FCSTD DOCUMENT  (FreeCAD 0.20R29177 +426 (Git))
Label: layout
License: All rights reserved
LicenseURL: http://en.wikipedia.org/wiki/All_rights_reserved
objects: Sketcher::SketchObject×3
note: 3 computed .brp shape members not serialized (recipe doc carries the construction recipe); baked Part::Feature solids carry a one-line shape summary decoded from their .brp

FEATURE [Sketcher::SketchObject] Sketch
  FullyConstrained = true
  sketch-geometry (256):
    g0: Circle CenterX=165.971 CenterY=76.4159 CenterZ=0 NormalX=0 NormalY=0 NormalZ=1 AngleXU=0 Radius=12
    g1: Circle CenterX=195.971 CenterY=76.4159 CenterZ=0 NormalX=0 NormalY=0 NormalZ=1 AngleXU=0 Radius=12
    g2: Circle CenterX=165.971 CenterY=106.416 CenterZ=0 NormalX=0 NormalY=0 NormalZ=1 AngleXU=0 Radius=12
    g3: Circle CenterX=195.971 CenterY=106.416 CenterZ=0 NormalX=0 NormalY=0 NormalZ=1 AngleXU=0 Radius=12
    g4: Circle CenterX=225.019 CenterY=98.9159 CenterZ=0 NormalX=0 NormalY=0 NormalZ=1 AngleXU=0 Radius=12
    g5: Circle CenterX=225.019 CenterY=68.9159 CenterZ=0 NormalX=0 NormalY=0 NormalZ=1 AngleXU=0 Radius=12
    g6: Circle CenterX=139.99 CenterY=91.4159 CenterZ=0 NormalX=0 NormalY=0 NormalZ=1 AngleXU=0 Radius=12
    g7: Circle CenterX=139.99 CenterY=61.4159 CenterZ=0 NormalX=0 NormalY=0 NormalZ=1 AngleXU=0 Radius=12
    g8: Circle CenterX=114.01 CenterY=76.4159 CenterZ=0 NormalX=0 NormalY=0 NormalZ=1 AngleXU=0 Radius=12
    g9: Circle CenterX=88.0289 CenterY=91.4159 CenterZ=0 NormalX=0 NormalY=0 NormalZ=1 AngleXU=0 Radius=12
    g10: Circle CenterX=58.0289 CenterY=91.4159 CenterZ=0 NormalX=0 NormalY=0 NormalZ=1 AngleXU=0 Radius=12
    g11: Circle CenterX=127 CenterY=23.5841 CenterZ=0 NormalX=0 NormalY=0 NormalZ=1 AngleXU=0 Radius=15
    g12: LineSegment StartX=139.99 StartY=61.4159 StartZ=0 EndX=88.0289 EndY=91.4159 EndZ=0
    g13: LineSegment StartX=139.99 StartY=61.4159 StartZ=0 EndX=127 EndY=61.4159 EndZ=0
    g14: LineSegment StartX=127 StartY=61.4159 StartZ=0 EndX=114.01 EndY=61.4159 EndZ=0
    g15: LineSegment StartX=10 StartY=127 StartZ=0 EndX=244 EndY=127 EndZ=0
    g16: LineSegment StartX=254 StartY=117 StartZ=0 EndX=254 EndY=10 EndZ=0
    g17: LineSegment StartX=244 StartY=0 StartZ=0 EndX=10 EndY=0 EndZ=0
    g18: LineSegment StartX=0 StartY=10 StartZ=0 EndX=0 EndY=117 EndZ=0
    g19: LineSegment StartX=127 StartY=23.5841 StartZ=0 EndX=0 EndY=23.5841 EndZ=0
    g20: LineSegment StartX=127 StartY=23.5841 StartZ=0 EndX=254 EndY=23.5841 EndZ=0
    g21: LineSegment StartX=58.0289 StartY=91.4159 StartZ=0 EndX=88.0289 EndY=91.4159 EndZ=0
    g22: LineSegment StartX=114.01 StartY=76.4159 StartZ=0 EndX=139.99 EndY=91.4159 EndZ=0
    g23: LineSegment StartX=139.99 StartY=91.4159 StartZ=0 EndX=165.971 EndY=106.416 EndZ=0
    g24: LineSegment StartX=165.971 StartY=106.416 StartZ=0 EndX=195.971 EndY=106.416 EndZ=0
    g25: LineSegment StartX=195.971 StartY=106.416 StartZ=0 EndX=225.019 EndY=98.9159 EndZ=0
    g26: LineSegment StartX=225.019 StartY=98.9159 StartZ=0 EndX=225.019 EndY=68.9159 EndZ=0
    g27: LineSegment StartX=165.971 StartY=106.416 StartZ=0 EndX=165.971 EndY=76.4159 EndZ=0
    g28: LineSegment StartX=139.99 StartY=91.4159 StartZ=0 EndX=139.99 EndY=61.4159 EndZ=0
    g29: LineSegment StartX=139.99 StartY=61.4159 StartZ=0 EndX=127 EndY=23.5841 EndZ=0
    g30: Circle CenterX=28.9815 CenterY=83.9159 CenterZ=0 NormalX=0 NormalY=0 NormalZ=1 AngleXU=0 Radius=12
    g31: Circle CenterX=28.9815 CenterY=53.9159 CenterZ=0 NormalX=0 NormalY=0 NormalZ=1 AngleXU=0 Radius=12
    g32: Circle CenterX=58.0289 CenterY=61.4159 CenterZ=0 NormalX=0 NormalY=0 NormalZ=1 AngleXU=0 Radius=12
    g33: Circle CenterX=88.0289 CenterY=61.4159 CenterZ=0 NormalX=0 NormalY=0 NormalZ=1 AngleXU=0 Radius=12
    g34: LineSegment StartX=58.0289 StartY=91.4159 StartZ=0 EndX=28.9815 EndY=83.9159 EndZ=0
    g35: LineSegment StartX=28.9815 StartY=83.9159 StartZ=0 EndX=28.9815 EndY=53.9159 EndZ=0
    g36: LineSegment StartX=58.0289 StartY=91.4159 StartZ=0 EndX=58.0289 EndY=61.4159 EndZ=0
    g37: LineSegment StartX=88.0289 StartY=91.4159 StartZ=0 EndX=88.0289 EndY=61.4159 EndZ=0
    g38: ArcOfCircle CenterX=10 CenterY=117 CenterZ=0 NormalX=0 NormalY=0 NormalZ=1 AngleXU=0 Radius=10 StartAngle=1.5708 EndAngle=3.14159
    g39: ArcOfCircle CenterX=10 CenterY=10 CenterZ=0 NormalX=0 NormalY=0 NormalZ=1 AngleXU=0 Radius=10 StartAngle=3.14159 EndAngle=4.71239
    g40: ArcOfCircle CenterX=244 CenterY=10 CenterZ=0 NormalX=0 NormalY=0 NormalZ=1 AngleXU=0 Radius=10 StartAngle=4.71239 EndAngle=6.28319
    g41: ArcOfCircle CenterX=244 CenterY=117 CenterZ=0 NormalX=0 NormalY=0 NormalZ=1 AngleXU=0 Radius=10 StartAngle=0 EndAngle=1.5708
    g42: LineSegment StartX=127 StartY=8.58407 StartZ=0 EndX=127 EndY=0 EndZ=0
    g43: LineSegment StartX=165.971 StartY=118.416 StartZ=0 EndX=165.971 EndY=127 EndZ=0
    g44: LineSegment StartX=17.522 StartY=119.1 StartZ=0 EndX=44.422 EndY=119.1 EndZ=0
    g45: LineSegment StartX=44.422 StartY=119.1 StartZ=0 EndX=44.422 EndY=99.64 EndZ=0
    g46: LineSegment StartX=44.422 StartY=99.64 StartZ=0 EndX=17.522 EndY=99.64 EndZ=0
    g47: LineSegment StartX=17.522 StartY=99.64 StartZ=0 EndX=17.522 EndY=119.1 EndZ=0
    g48: Circle CenterX=157.215 CenterY=36.8533 CenterZ=0 NormalX=0 NormalY=0 NormalZ=1 AngleXU=0 Radius=12
    g49: Circle CenterX=94.1366 CenterY=26.5841 CenterZ=0 NormalX=0 NormalY=0 NormalZ=1 AngleXU=0 Radius=12
    g50: LineSegment StartX=94.1366 StartY=26.5841 StartZ=0 EndX=127 EndY=23.5841 EndZ=0
    g51: LineSegment StartX=109.54 StartY=127 StartZ=0 EndX=118.48 EndY=127 EndZ=0
    g52: LineSegment StartX=118.48 StartY=127 StartZ=0 EndX=118.48 EndY=119.41 EndZ=0
    g53: LineSegment StartX=118.48 StartY=119.41 StartZ=0 EndX=109.54 EndY=119.41 EndZ=0
    g54: LineSegment StartX=109.54 StartY=119.41 StartZ=0 EndX=109.54 EndY=127 EndZ=0
    g55: LineSegment StartX=81.9846 StartY=127 StartZ=0 EndX=95.2346 EndY=127 EndZ=0
    g56: LineSegment StartX=95.2346 StartY=127 StartZ=0 EndX=95.2346 EndY=118.4 EndZ=0
    g57: LineSegment StartX=95.2346 StartY=118.4 StartZ=0 EndX=81.9846 EndY=118.4 EndZ=0
    g58: LineSegment StartX=81.9846 StartY=118.4 StartZ=0 EndX=81.9846 EndY=127 EndZ=0
    g59: LineSegment StartX=17.522 StartY=127 StartZ=0 EndX=25.372 EndY=127 EndZ=0
    g60: LineSegment StartX=25.372 StartY=127 StartZ=0 EndX=25.372 EndY=123.25 EndZ=0
    g61: LineSegment StartX=25.372 StartY=123.25 StartZ=0 EndX=17.522 EndY=123.25 EndZ=0
    g62: LineSegment StartX=17.522 StartY=123.25 StartZ=0 EndX=17.522 EndY=127 EndZ=0
    g63: LineSegment StartX=20 StartY=117 StartZ=0 EndX=41.744 EndY=117 EndZ=0
    g64: LineSegment StartX=41.744 StartY=117 StartZ=0 EndX=41.744 EndY=106.136 EndZ=0
    g65: LineSegment StartX=41.744 StartY=106.136 StartZ=0 EndX=20 EndY=106.136 EndZ=0
    g66: LineSegment StartX=20 StartY=106.136 StartZ=0 EndX=20 EndY=117 EndZ=0
    g67: LineSegment StartX=109.54 StartY=124.41 StartZ=0 EndX=114.01 EndY=124.41 EndZ=0
    g68: LineSegment StartX=114.01 StartY=124.41 StartZ=0 EndX=118.48 EndY=124.41 EndZ=0
    g69: LineSegment StartX=95.2346 StartY=123.4 StartZ=0 EndX=88.6096 EndY=123.4 EndZ=0
    g70: LineSegment StartX=88.6096 StartY=123.4 StartZ=0 EndX=81.9846 EndY=123.4 EndZ=0
    g71: LineSegment StartX=88.0289 StartY=61.4159 StartZ=0 EndX=94.1366 EndY=26.5841 EndZ=0
    g72: LineSegment StartX=157.215 StartY=36.8533 StartZ=0 EndX=127 EndY=23.5841 EndZ=0
    g73: LineSegment StartX=139.99 StartY=61.4159 StartZ=0 EndX=157.215 EndY=36.8533 EndZ=0
    g74: LineSegment StartX=36.572 StartY=127 StartZ=0 EndX=44.422 EndY=127 EndZ=0
    g75: LineSegment StartX=44.422 StartY=127 StartZ=0 EndX=44.422 EndY=123.25 EndZ=0
    g76: LineSegment StartX=44.422 StartY=123.25 StartZ=0 EndX=36.572 EndY=123.25 EndZ=0
    g77: LineSegment StartX=36.572 StartY=123.25 StartZ=0 EndX=36.572 EndY=127 EndZ=0
    g78: Circle CenterX=10 CenterY=117 CenterZ=0 NormalX=0 NormalY=0 NormalZ=1 AngleXU=0 Radius=2
    g79: Circle CenterX=244 CenterY=117 CenterZ=0 NormalX=0 NormalY=0 NormalZ=1 AngleXU=0 Radius=2
    g80: Circle CenterX=244 CenterY=10 CenterZ=0 NormalX=0 NormalY=0 NormalZ=1 AngleXU=0 Radius=2
    g81: Circle CenterX=10 CenterY=10 CenterZ=0 NormalX=0 NormalY=0 NormalZ=1 AngleXU=0 Radius=2
    g82: Circle CenterX=109.191 CenterY=10 CenterZ=0 NormalX=0 NormalY=0 NormalZ=1 AngleXU=0 Radius=2
    g83: Circle CenterX=144.809 CenterY=117 CenterZ=0 NormalX=0 NormalY=0 NormalZ=1 AngleXU=0 Radius=2
    g84: LineSegment StartX=127 StartY=23.5841 StartZ=0 EndX=109.191 EndY=10 EndZ=0
    g85: LineSegment StartX=109.191 StartY=10 StartZ=0 EndX=94.1366 EndY=26.5841 EndZ=0
    g86: LineSegment StartX=144.809 StartY=117 StartZ=0 EndX=127 EndY=117 EndZ=0
    g87: LineSegment StartX=109.191 StartY=10 StartZ=0 EndX=127 EndY=10 EndZ=0
    g88: LineSegment StartX=23.172 StartY=98.48 StartZ=0 EndX=38.772 EndY=98.48 EndZ=0
    g89: LineSegment StartX=38.772 StartY=98.48 StartZ=0 EndX=44.422 EndY=98.48 EndZ=0
    g90: LineSegment StartX=23.172 StartY=98.48 StartZ=0 EndX=17.522 EndY=98.48 EndZ=0
    g91: LineSegment StartX=23.172 StartY=98.48 StartZ=0 EndX=23.172 EndY=108.71 EndZ=0
    g92: LineSegment StartX=23.172 StartY=108.71 StartZ=0 EndX=38.772 EndY=108.71 EndZ=0
    g93: LineSegment StartX=38.772 StartY=108.71 StartZ=0 EndX=38.772 EndY=98.48 EndZ=0
    g94: ArcOfCircle CenterX=23.172 CenterY=98.48 CenterZ=0 NormalX=0 NormalY=0 NormalZ=1 AngleXU=0 Radius=0.5 StartAngle=1.5708 EndAngle=4.71239
    g95: ArcOfCircle CenterX=38.772 CenterY=98.48 CenterZ=0 NormalX=0 NormalY=0 NormalZ=1 AngleXU=0 Radius=0.5 StartAngle=4.71239 EndAngle=7.85398
    g96: LineSegment StartX=23.172 StartY=97.98 StartZ=0 EndX=38.772 EndY=97.98 EndZ=0
    g97: LineSegment StartX=23.172 StartY=98.98 StartZ=0 EndX=38.772 EndY=98.98 EndZ=0
    g98: Circle CenterX=10 CenterY=117 CenterZ=0 NormalX=0 NormalY=0 NormalZ=1 AngleXU=0 Radius=1.3
    g99: Circle CenterX=144.809 CenterY=117 CenterZ=0 NormalX=0 NormalY=0 NormalZ=1 AngleXU=0 Radius=1.3
    g100: Circle CenterX=244 CenterY=117 CenterZ=0 NormalX=0 NormalY=0 NormalZ=1 AngleXU=0 Radius=1.3
    g101: Circle CenterX=244 CenterY=10 CenterZ=0 NormalX=0 NormalY=0 NormalZ=1 AngleXU=0 Radius=1.3
    g102: Circle CenterX=109.191 CenterY=10 CenterZ=0 NormalX=0 NormalY=0 NormalZ=1 AngleXU=0 Radius=1.3
    g103: Circle CenterX=10 CenterY=10 CenterZ=0 NormalX=0 NormalY=0 NormalZ=1 AngleXU=0 Radius=1.3
    g104: LineSegment StartX=17.522 StartY=119.6 StartZ=0 EndX=44.422 EndY=119.6 EndZ=0
    g105: LineSegment StartX=44.922 StartY=119.1 StartZ=0 EndX=44.922 EndY=98.48 EndZ=0
    g106: LineSegment StartX=44.422 StartY=97.98 StartZ=0 EndX=17.522 EndY=97.98 EndZ=0
    g107: LineSegment StartX=17.022 StartY=98.48 StartZ=0 EndX=17.022 EndY=119.1 EndZ=0
    g108: ArcOfCircle CenterX=44.422 CenterY=119.1 CenterZ=0 NormalX=0 NormalY=0 NormalZ=1 AngleXU=0 Radius=0.5 StartAngle=7.2e-15 EndAngle=1.5708
    g109: ArcOfCircle CenterX=44.422 CenterY=98.48 CenterZ=0 NormalX=0 NormalY=0 NormalZ=1 AngleXU=0 Radius=0.5 StartAngle=4.71239 EndAngle=6.28319
    g110: ArcOfCircle CenterX=17.522 CenterY=98.48 CenterZ=0 NormalX=0 NormalY=0 NormalZ=1 AngleXU=0 Radius=0.5 StartAngle=3.14159 EndAngle=4.71239
    g111: ArcOfCircle CenterX=17.522 CenterY=119.1 CenterZ=0 NormalX=0 NormalY=0 NormalZ=1 AngleXU=0 Radius=0.5 StartAngle=1.5708 EndAngle=3.14159
    g112: Circle CenterX=28.9815 CenterY=83.9159 CenterZ=0 NormalX=0 NormalY=0 NormalZ=1 AngleXU=0 Radius=11
    g113: Circle CenterX=58.0289 CenterY=91.4159 CenterZ=0 NormalX=0 NormalY=0 NormalZ=1 AngleXU=0 Radius=11
    g114: Circle CenterX=28.9815 CenterY=53.9159 CenterZ=0 NormalX=0 NormalY=0 NormalZ=1 AngleXU=0 Radius=11
    g115: Circle CenterX=58.0289 CenterY=61.4159 CenterZ=0 NormalX=0 NormalY=0 NormalZ=1 AngleXU=0 Radius=11
    g116: Circle CenterX=88.0289 CenterY=61.4159 CenterZ=0 NormalX=0 NormalY=0 NormalZ=1 AngleXU=0 Radius=11
    g117: Circle CenterX=88.0289 CenterY=91.4159 CenterZ=0 NormalX=0 NormalY=0 NormalZ=1 AngleXU=0 Radius=11
    g118: Circle CenterX=114.01 CenterY=76.4159 CenterZ=0 NormalX=0 NormalY=0 NormalZ=1 AngleXU=0 Radius=11
    g119: Circle CenterX=139.99 CenterY=91.4159 CenterZ=0 NormalX=0 NormalY=0 NormalZ=1 AngleXU=0 Radius=11
    g120: Circle CenterX=139.99 CenterY=61.4159 CenterZ=0 NormalX=0 NormalY=0 NormalZ=1 AngleXU=0 Radius=11
    g121: Circle CenterX=94.1366 CenterY=26.5841 CenterZ=0 NormalX=0 NormalY=0 NormalZ=1 AngleXU=0 Radius=11
    g122: Circle CenterX=157.215 CenterY=36.8533 CenterZ=0 NormalX=0 NormalY=0 NormalZ=1 AngleXU=0 Radius=11
    g123: Circle CenterX=165.971 CenterY=106.416 CenterZ=0 NormalX=0 NormalY=0 NormalZ=1 AngleXU=0 Radius=11
    g124: Circle CenterX=165.971 CenterY=76.4159 CenterZ=0 NormalX=0 NormalY=0 NormalZ=1 AngleXU=0 Radius=11
    g125: Circle CenterX=195.971 CenterY=76.4159 CenterZ=0 NormalX=0 NormalY=0 NormalZ=1 AngleXU=0 Radius=11
    g126: Circle CenterX=195.971 CenterY=106.416 CenterZ=0 NormalX=0 NormalY=0 NormalZ=1 AngleXU=0 Radius=11
    g127: Circle CenterX=225.019 CenterY=98.9159 CenterZ=0 NormalX=0 NormalY=0 NormalZ=1 AngleXU=0 Radius=11
    g128: Circle CenterX=225.019 CenterY=68.9159 CenterZ=0 NormalX=0 NormalY=0 NormalZ=1 AngleXU=0 Radius=11
    g129: Circle CenterX=127 CenterY=23.5841 CenterZ=0 NormalX=0 NormalY=0 NormalZ=1 AngleXU=0 Radius=13.5
    g130: LineSegment StartX=132.99 StartY=98.4159 StartZ=0 EndX=146.99 EndY=98.4159 EndZ=0
    g131: LineSegment StartX=146.99 StartY=98.4159 StartZ=0 EndX=146.99 EndY=84.4159 EndZ=0
    g132: LineSegment StartX=146.99 StartY=84.4159 StartZ=0 EndX=132.99 EndY=84.4159 EndZ=0
    g133: LineSegment StartX=132.99 StartY=84.4159 StartZ=0 EndX=132.99 EndY=98.4159 EndZ=0
    g134: LineSegment StartX=132.99 StartY=98.4159 StartZ=0 EndX=139.99 EndY=91.4159 EndZ=0
    g135: LineSegment StartX=132.99 StartY=84.4159 StartZ=0 EndX=139.99 EndY=91.4159 EndZ=0
    g136: LineSegment StartX=146.99 StartY=98.4159 StartZ=0 EndX=139.99 EndY=91.4159 EndZ=0
    g137: LineSegment StartX=146.99 StartY=68.4159 StartZ=0 EndX=139.99 EndY=61.4159 EndZ=0
    g138: LineSegment StartX=132.99 StartY=68.4159 StartZ=0 EndX=139.99 EndY=61.4159 EndZ=0
    g139: LineSegment StartX=132.99 StartY=54.4159 StartZ=0 EndX=139.99 EndY=61.4159 EndZ=0
    g140: LineSegment StartX=132.99 StartY=68.4159 StartZ=0 EndX=146.99 EndY=68.4159 EndZ=0
    g141: LineSegment StartX=132.99 StartY=54.4159 StartZ=0 EndX=132.99 EndY=68.4159 EndZ=0
    g142: LineSegment StartX=146.99 StartY=68.4159 StartZ=0 EndX=146.99 EndY=54.4159 EndZ=0
    g143: LineSegment StartX=146.99 StartY=54.4159 StartZ=0 EndX=132.99 EndY=54.4159 EndZ=0
    g144: LineSegment StartX=158.971 StartY=99.4159 StartZ=0 EndX=158.971 EndY=113.416 EndZ=0
    g145: LineSegment StartX=158.971 StartY=113.416 StartZ=0 EndX=172.971 EndY=113.416 EndZ=0
    g146: LineSegment StartX=172.971 StartY=113.416 StartZ=0 EndX=172.971 EndY=99.4159 EndZ=0
    g147: LineSegment StartX=172.971 StartY=99.4159 StartZ=0 EndX=158.971 EndY=99.4159 EndZ=0
    g148: LineSegment StartX=158.971 StartY=99.4159 StartZ=0 EndX=165.971 EndY=106.416 EndZ=0
    g149: LineSegment StartX=158.971 StartY=113.416 StartZ=0 EndX=165.971 EndY=106.416 EndZ=0
    g150: LineSegment StartX=172.971 StartY=113.416 StartZ=0 EndX=165.971 EndY=106.416 EndZ=0
    g151: LineSegment StartX=202.971 StartY=99.4159 StartZ=0 EndX=188.971 EndY=99.4159 EndZ=0
    g152: LineSegment StartX=188.971 StartY=99.4159 StartZ=0 EndX=188.971 EndY=113.416 EndZ=0
    g153: LineSegment StartX=188.971 StartY=113.416 StartZ=0 EndX=202.971 EndY=113.416 EndZ=0
    g154: LineSegment StartX=202.971 StartY=113.416 StartZ=0 EndX=202.971 EndY=99.4159 EndZ=0
    g155: LineSegment StartX=202.971 StartY=113.416 StartZ=0 EndX=195.971 EndY=106.416 EndZ=0
    g156: LineSegment StartX=188.971 StartY=113.416 StartZ=0 EndX=195.971 EndY=106.416 EndZ=0
    g157: LineSegment StartX=188.971 StartY=99.4159 StartZ=0 EndX=195.971 EndY=106.416 EndZ=0
    g158: LineSegment StartX=158.971 StartY=69.4159 StartZ=0 EndX=158.971 EndY=83.4159 EndZ=0
    g159: LineSegment StartX=172.971 StartY=69.4159 StartZ=0 EndX=158.971 EndY=69.4159 EndZ=0
    g160: LineSegment StartX=158.971 StartY=83.4159 StartZ=0 EndX=172.971 EndY=83.4159 EndZ=0
    g161: LineSegment StartX=172.971 StartY=83.4159 StartZ=0 EndX=172.971 EndY=69.4159 EndZ=0
    g162: LineSegment StartX=172.971 StartY=83.4159 StartZ=0 EndX=165.971 EndY=76.4159 EndZ=0
    g163: LineSegment StartX=158.971 StartY=83.4159 StartZ=0 EndX=165.971 EndY=76.4159 EndZ=0
    g164: LineSegment StartX=158.971 StartY=69.4159 StartZ=0 EndX=165.971 EndY=76.4159 EndZ=0
    g165: LineSegment StartX=188.971 StartY=69.4159 StartZ=0 EndX=188.971 EndY=83.4159 EndZ=0
    g166: LineSegment StartX=202.971 StartY=69.4159 StartZ=0 EndX=188.971 EndY=69.4159 EndZ=0
    g167: LineSegment StartX=188.971 StartY=83.4159 StartZ=0 EndX=202.971 EndY=83.4159 EndZ=0
    g168: LineSegment StartX=202.971 StartY=83.4159 StartZ=0 EndX=202.971 EndY=69.4159 EndZ=0
    g169: LineSegment StartX=202.971 StartY=83.4159 StartZ=0 EndX=195.971 EndY=76.4159 EndZ=0
    g170: LineSegment StartX=188.971 StartY=83.4159 StartZ=0 EndX=195.971 EndY=76.4159 EndZ=0
    g171: LineSegment StartX=188.971 StartY=69.4159 StartZ=0 EndX=195.971 EndY=76.4159 EndZ=0
    g172: LineSegment StartX=218.019 StartY=91.9159 StartZ=0 EndX=218.019 EndY=105.916 EndZ=0
    g173: LineSegment StartX=232.019 StartY=91.9159 StartZ=0 EndX=218.019 EndY=91.9159 EndZ=0
    g174: LineSegment StartX=218.019 StartY=105.916 StartZ=0 EndX=232.019 EndY=105.916 EndZ=0
    g175: LineSegment StartX=232.019 StartY=105.916 StartZ=0 EndX=232.019 EndY=91.9159 EndZ=0
    g176: LineSegment StartX=232.019 StartY=105.916 StartZ=0 EndX=225.019 EndY=98.9159 EndZ=0
    g177: LineSegment StartX=218.019 StartY=105.916 StartZ=0 EndX=225.019 EndY=98.9159 EndZ=0
    g178: LineSegment StartX=218.019 StartY=91.9159 StartZ=0 EndX=225.019 EndY=98.9159 EndZ=0
    g179: LineSegment StartX=218.019 StartY=61.9159 StartZ=0 EndX=218.019 EndY=75.9159 EndZ=0
    g180: LineSegment StartX=232.019 StartY=61.9159 StartZ=0 EndX=218.019 EndY=61.9159 EndZ=0
    g181: LineSegment StartX=218.019 StartY=75.9159 StartZ=0 EndX=232.019 EndY=75.9159 EndZ=0
    g182: LineSegment StartX=232.019 StartY=75.9159 StartZ=0 EndX=232.019 EndY=61.9159 EndZ=0
    g183: LineSegment StartX=232.019 StartY=75.9159 StartZ=0 EndX=225.019 EndY=68.9159 EndZ=0
    g184: LineSegment StartX=218.019 StartY=75.9159 StartZ=0 EndX=225.019 EndY=68.9159 EndZ=0
    g185: LineSegment StartX=218.019 StartY=61.9159 StartZ=0 EndX=225.019 EndY=68.9159 EndZ=0
    g186: LineSegment StartX=150.215 StartY=29.8533 StartZ=0 EndX=150.215 EndY=43.8533 EndZ=0
    g187: LineSegment StartX=164.215 StartY=29.8533 StartZ=0 EndX=150.215 EndY=29.8533 EndZ=0
    g188: LineSegment StartX=150.215 StartY=43.8533 StartZ=0 EndX=164.215 EndY=43.8533 EndZ=0
    g189: LineSegment StartX=164.215 StartY=43.8533 StartZ=0 EndX=164.215 EndY=29.8533 EndZ=0
    g190: LineSegment StartX=164.215 StartY=43.8533 StartZ=0 EndX=157.215 EndY=36.8533 EndZ=0
    g191: LineSegment StartX=150.215 StartY=43.8533 StartZ=0 EndX=157.215 EndY=36.8533 EndZ=0
    g192: LineSegment StartX=150.215 StartY=29.8533 StartZ=0 EndX=157.215 EndY=36.8533 EndZ=0
    g193: LineSegment StartX=107.01 StartY=69.4159 StartZ=0 EndX=107.01 EndY=83.4159 EndZ=0
    g194: LineSegment StartX=121.01 StartY=69.4159 StartZ=0 EndX=107.01 EndY=69.4159 EndZ=0
    g195: LineSegment StartX=107.01 StartY=83.4159 StartZ=0 EndX=121.01 EndY=83.4159 EndZ=0
    g196: LineSegment StartX=121.01 StartY=83.4159 StartZ=0 EndX=121.01 EndY=69.4159 EndZ=0
    g197: LineSegment StartX=121.01 StartY=83.4159 StartZ=0 EndX=114.01 EndY=76.4159 EndZ=0
    g198: LineSegment StartX=107.01 StartY=83.4159 StartZ=0 EndX=114.01 EndY=76.4159 EndZ=0
    g199: LineSegment StartX=107.01 StartY=69.4159 StartZ=0 EndX=114.01 EndY=76.4159 EndZ=0
    g200: LineSegment StartX=120 StartY=16.5841 StartZ=0 EndX=120 EndY=30.5841 EndZ=0
    g201: LineSegment StartX=134 StartY=16.5841 StartZ=0 EndX=120 EndY=16.5841 EndZ=0
    g202: LineSegment StartX=120 StartY=30.5841 StartZ=0 EndX=134 EndY=30.5841 EndZ=0
    g203: LineSegment StartX=134 StartY=30.5841 StartZ=0 EndX=134 EndY=16.5841 EndZ=0
    g204: LineSegment StartX=134 StartY=30.5841 StartZ=0 EndX=127 EndY=23.5841 EndZ=0
    g205: LineSegment StartX=120 StartY=30.5841 StartZ=0 EndX=127 EndY=23.5841 EndZ=0
    g206: LineSegment StartX=120 StartY=16.5841 StartZ=0 EndX=127 EndY=23.5841 EndZ=0
    g207: LineSegment StartX=81.0289 StartY=84.4159 StartZ=0 EndX=81.0289 EndY=98.4159 EndZ=0
    g208: LineSegment StartX=95.0289 StartY=84.4159 StartZ=0 EndX=81.0289 EndY=84.4159 EndZ=0
    g209: LineSegment StartX=81.0289 StartY=98.4159 StartZ=0 EndX=95.0289 EndY=98.4159 EndZ=0
    g210: LineSegment StartX=95.0289 StartY=98.4159 StartZ=0 EndX=95.0289 EndY=84.4159 EndZ=0
    g211: LineSegment StartX=95.0289 StartY=98.4159 StartZ=0 EndX=88.0289 EndY=91.4159 EndZ=0
    g212: LineSegment StartX=81.0289 StartY=98.4159 StartZ=0 EndX=88.0289 EndY=91.4159 EndZ=0
    g213: LineSegment StartX=81.0289 StartY=84.4159 StartZ=0 EndX=88.0289 EndY=91.4159 EndZ=0
    g214: LineSegment StartX=81.0289 StartY=54.4159 StartZ=0 EndX=81.0289 EndY=68.4159 EndZ=0
    g215: LineSegment StartX=95.0289 StartY=54.4159 StartZ=0 EndX=81.0289 EndY=54.4159 EndZ=0
    g216: LineSegment StartX=81.0289 StartY=68.4159 StartZ=0 EndX=95.0289 EndY=68.4159 EndZ=0
    g217: LineSegment StartX=95.0289 StartY=68.4159 StartZ=0 EndX=95.0289 EndY=54.4159 EndZ=0
    g218: LineSegment StartX=95.0289 StartY=68.4159 StartZ=0 EndX=88.0289 EndY=61.4159 EndZ=0
    g219: LineSegment StartX=81.0289 StartY=68.4159 StartZ=0 EndX=88.0289 EndY=61.4159 EndZ=0
    g220: LineSegment StartX=81.0289 StartY=54.4159 StartZ=0 EndX=88.0289 EndY=61.4159 EndZ=0
    g221: LineSegment StartX=87.1366 StartY=19.5841 StartZ=0 EndX=87.1366 EndY=33.5841 EndZ=0
    g222: LineSegment StartX=101.137 StartY=19.5841 StartZ=0 EndX=87.1366 EndY=19.5841 EndZ=0
    g223: LineSegment StartX=87.1366 StartY=33.5841 StartZ=0 EndX=101.137 EndY=33.5841 EndZ=0
    g224: LineSegment StartX=101.137 StartY=33.5841 StartZ=0 EndX=101.137 EndY=19.5841 EndZ=0
    g225: LineSegment StartX=101.137 StartY=33.5841 StartZ=0 EndX=94.1366 EndY=26.5841 EndZ=0
    g226: LineSegment StartX=87.1366 StartY=33.5841 StartZ=0 EndX=94.1366 EndY=26.5841 EndZ=0
    g227: LineSegment StartX=87.1366 StartY=19.5841 StartZ=0 EndX=94.1366 EndY=26.5841 EndZ=0
    g228: LineSegment StartX=51.0289 StartY=84.4159 StartZ=0 EndX=51.0289 EndY=98.4159 EndZ=0
    g229: LineSegment StartX=65.0289 StartY=84.4159 StartZ=0 EndX=51.0289 EndY=84.4159 EndZ=0
    g230: LineSegment StartX=51.0289 StartY=98.4159 StartZ=0 EndX=65.0289 EndY=98.4159 EndZ=0
    g231: LineSegment StartX=65.0289 StartY=98.4159 StartZ=0 EndX=65.0289 EndY=84.4159 EndZ=0
    g232: LineSegment StartX=65.0289 StartY=98.4159 StartZ=0 EndX=58.0289 EndY=91.4159 EndZ=0
    g233: LineSegment StartX=51.0289 StartY=98.4159 StartZ=0 EndX=58.0289 EndY=91.4159 EndZ=0
    g234: LineSegment StartX=51.0289 StartY=84.4159 StartZ=0 EndX=58.0289 EndY=91.4159 EndZ=0
    g235: LineSegment StartX=51.0289 StartY=54.4159 StartZ=0 EndX=51.0289 EndY=68.4159 EndZ=0
    g236: LineSegment StartX=65.0289 StartY=54.4159 StartZ=0 EndX=51.0289 EndY=54.4159 EndZ=0
    g237: LineSegment StartX=51.0289 StartY=68.4159 StartZ=0 EndX=65.0289 EndY=68.4159 EndZ=0
    g238: LineSegment StartX=65.0289 StartY=68.4159 StartZ=0 EndX=65.0289 EndY=54.4159 EndZ=0
    g239: LineSegment StartX=65.0289 StartY=68.4159 StartZ=0 EndX=58.0289 EndY=61.4159 EndZ=0
    g240: LineSegment StartX=51.0289 StartY=68.4159 StartZ=0 EndX=58.0289 EndY=61.4159 EndZ=0
    g241: LineSegment StartX=51.0289 StartY=54.4159 StartZ=0 EndX=58.0289 EndY=61.4159 EndZ=0
    g242: LineSegment StartX=21.9815 StartY=76.9159 StartZ=0 EndX=21.9815 EndY=90.9159 EndZ=0
    g243: LineSegment StartX=35.9815 StartY=76.9159 StartZ=0 EndX=21.9815 EndY=76.9159 EndZ=0
    g244: LineSegment StartX=21.9815 StartY=90.9159 StartZ=0 EndX=35.9815 EndY=90.9159 EndZ=0
    g245: LineSegment StartX=35.9815 StartY=90.9159 StartZ=0 EndX=35.9815 EndY=76.9159 EndZ=0
    g246: LineSegment StartX=35.9815 StartY=90.9159 StartZ=0 EndX=28.9815 EndY=83.9159 EndZ=0
    g247: LineSegment StartX=21.9815 StartY=90.9159 StartZ=0 EndX=28.9815 EndY=83.9159 EndZ=0
    g248: LineSegment StartX=21.9815 StartY=76.9159 StartZ=0 EndX=28.9815 EndY=83.9159 EndZ=0
    g249: LineSegment StartX=21.9815 StartY=46.9159 StartZ=0 EndX=21.9815 EndY=60.9159 EndZ=0
    g250: LineSegment StartX=35.9815 StartY=46.9159 StartZ=0 EndX=21.9815 EndY=46.9159 EndZ=0
    g251: LineSegment StartX=21.9815 StartY=60.9159 StartZ=0 EndX=35.9815 EndY=60.9159 EndZ=0
    g252: LineSegment StartX=35.9815 StartY=60.9159 StartZ=0 EndX=35.9815 EndY=46.9159 EndZ=0
    g253: LineSegment StartX=35.9815 StartY=60.9159 StartZ=0 EndX=28.9815 EndY=53.9159 EndZ=0
    g254: LineSegment StartX=21.9815 StartY=60.9159 StartZ=0 EndX=28.9815 EndY=53.9159 EndZ=0
    g255: LineSegment StartX=21.9815 StartY=46.9159 StartZ=0 EndX=28.9815 EndY=53.9159 EndZ=0
  constraints (654):
    c: Radius(g6) = 12
    c: Equal(g6,g7)
    c: Equal(g6,g2)
    c: Equal(g6,g0)
    c: Equal(g6,g3)
    c: Equal(g6,g1)
    c: Equal(g6,g4)
    c: Equal(g6,g5)
    c: Equal(g6,g8)
    c: Equal(g6,g9)
    c: Equal(g6,g10)
    c: Radius(g11) = 15
    c: Horizontal(g2,g3)
    c: Horizontal(g0,g1)
    c: Vertical(g2,g0)
    c: Vertical(g3,g1)
    c: Vertical(g4,g5)
    c: Vertical(g6,g7)
    c: DistanceY(g4,g3) = 7.5
    c: DistanceY(g6,g2) = 15
    c: Coincident(g12,g7)
    c: Coincident(g12,g9)
    c: PointOnObject(g8,g12)
    c: Horizontal(g9,g10)
    c: Coincident(g13,g7)
    c: Horizontal(g13)
    c: Coincident(g14,g13)
    c: Horizontal(g14)
    c: Vertical(g14,g8)
    c: Equal(g13,g14)
    c: Vertical(g13,g11)
    c: Distance(g7,g11) = 40
    c: Horizontal(g15)
    c: Horizontal(g17)
    c: Vertical(g16)
    c: Vertical(g18)
    c: Coincident(g19,g11)
    c: PointOnObject(g19,g18)
    c: Horizontal(g19)
    c: Coincident(g20,g11)
    c: PointOnObject(g20,g16)
    c: Horizontal(g20)
    c: Equal(g20,g19)
    c: Coincident(g21,g10)
    c: Coincident(g21,g9)
    c: Coincident(g22,g8)
    c: Coincident(g22,g6)
    c: Coincident(g23,g6)
    c: Coincident(g23,g2)
    c: Coincident(g24,g2)
    c: Coincident(g24,g3)
    c: Coincident(g25,g3)
    c: Coincident(g25,g4)
    c: Coincident(g26,g4)
    c: Coincident(g26,g5)
    c: Coincident(g27,g2)
    c: Coincident(g27,g0)
    c: Coincident(g28,g6)
    c: Coincident(g28,g7)
    c: Coincident(g29,g7)
    c: Coincident(g29,g11)
    c: Distance(g23) = 30
    c: Equal(g23,g24)
    c: Equal(g23,g25)
    c: Equal(g23,g27)
    c: Equal(g23,g26)
    c: Equal(g23,g22)
    c: Equal(g23,g28)
    c: Equal(g23,g21)
    c: Horizontal(g9,g6)
    c: PointOnObject(g8,g23)
    c: Equal(g6,g30)
    c: Equal(g6,g31)
    c: Equal(g6,g32)
    c: DistanceY(g30,g10) = 7.5
    c: Coincident(g34,g10)
    c: Coincident(g34,g30)
    c: Coincident(g35,g30)
    c: Coincident(g35,g31)
    c: Vertical(g31,g30)
    c: Equal(g6,g33)
    c: Vertical(g32,g10)
    c: Coincident(g36,g10)
    c: Coincident(g36,g32)
    c: Coincident(g37,g9)
    c: Coincident(g37,g33)
    c: Vertical(g9,g33)
    c: Equal(g23, g34-g37) x4
    c: Tangent(g15,g38) = 1.5708
    c: Tangent(g18,g38) = 1.5708
    c: Tangent(g17,g39) = 1.5708
    c: Tangent(g18,g39) = 1.5708
    c: Tangent(g16,g40) = 1.5708
    c: Tangent(g17,g40) = 1.5708
    c: Tangent(g15,g41) = 1.5708
    c: Tangent(g16,g41) = 1.5708
    c: Equal(g39,g38)
    c: Equal(g39,g40)
    c: Equal(g39,g41)
    c: Radius(g39) = 10
    c: PointOnObject(g42,g11)
    c: PointOnObject(g42,g17)
    c: Perpendicular(g11,g42)
    c: Vertical(g42)
    c: DistanceY(g17,g15) = 127
    c: DistanceX(g18,g16) = 254
    c: PointOnObject(g43,g2)
    c: PointOnObject(g43,g15)
    c: Vertical(g43)
    c: Perpendicular(g2,g43)
    c: Equal(g43,g42)
    c: Coincident(g44,g45)
    c: Coincident(g45,g46)
    c: Coincident(g46,g47)
    c: Coincident(g47,g44)
    c: Horizontal(g44)
    c: Horizontal(g46)
    c: Vertical(g45)
    c: Vertical(g47)
    c: DistanceX(g46,g46) = 26.9
    c: DistanceY(g47,g47) = 19.46
    c: PointOnObject(g18,g-2)
    c: PointOnObject(g17,g-1)
    c: Equal(g6,g48)
    c: Equal(g6,g49)
    c: Coincident(g50,g49)
    c: Coincident(g50,g11)
    c: Distance(g50) = 33
    c: DistanceY(g11,g49) = 3
    c: Coincident(g51,g52)
    c: Coincident(g52,g53)
    c: Coincident(g53,g54)
    c: Coincident(g54,g51)
    c: Horizontal(g51)
    c: Horizontal(g53)
    c: Vertical(g52)
    c: Vertical(g54)
    c: PointOnObject(g51,g15)
    c: DistanceX(g53,g53) = 8.94
    c: DistanceY(g54,g54) = 7.59
    c: Coincident(g55,g56)
    c: Coincident(g56,g57)
    c: Coincident(g57,g58)
    c: Coincident(g58,g55)
    c: Horizontal(g55)
    c: Horizontal(g57)
    c: Vertical(g56)
    c: Vertical(g58)
    c: DistanceX(g57,g57) = 13.25
    c: DistanceY(g58,g58) = 8.6
    c: Coincident(g59,g60)
    c: Coincident(g60,g61)
    c: Coincident(g61,g62)
    c: Coincident(g62,g59)
    c: Horizontal(g59)
    c: Horizontal(g61)
    c: Vertical(g60)
    c: Vertical(g62)
    c: DistanceX(g61,g61) = 7.85
    c: DistanceY(g62,g62) = 3.75
    c: PointOnObject(g55,g15)
    c: PointOnObject(g59,g15)
    c: Coincident(g63,g64)
    c: Coincident(g64,g65)
    c: Coincident(g65,g66)
    c: Coincident(g66,g63)
    c: Horizontal(g63)
    c: Horizontal(g65)
    c: Vertical(g64)
    c: Vertical(g66)
    c: DistanceY(g66,g66) = 10.864
    c: DistanceX(g63,g63) = 21.744
    c: DistanceY(g63,g44) = 2.1
    c: DistanceX(g44,g63) = 2.478
    c: PointOnObject(g67,g54)
    c: Horizontal(g67)
    c: Coincident(g68,g67)
    c: PointOnObject(g68,g52)
    c: PointOnObject(g69,g56)
    c: Coincident(g70,g69)
    c: PointOnObject(g70,g58)
    c: Horizontal(g70)
    c: Horizontal(g69)
    c: Horizontal(g68)
    c: Equal(g68,g67)
    c: Equal(g69,g70)
    c: DistanceX(g69,g67) = 25.4
    c: DistanceY(g63,g15) = 10
    c: DistanceX(g18,g63) = 20
    c: Vertical(g67,g8)
    c: Coincident(g71,g33)
    c: Coincident(g71,g49)
    c: Coincident(g72,g48)
    c: Coincident(g72,g11)
    c: Equal(g50,g72)
    c: Coincident(g73,g7)
    c: Coincident(g73,g48)
    c: Equal(g73,g23)
    c: Coincident(g74,g75)
    c: Coincident(g75,g76)
    c: Coincident(g76,g77)
    c: Coincident(g77,g74)
    c: Horizontal(g74)
    c: Horizontal(g76)
    c: Vertical(g75)
    c: Vertical(g77)
    c: Equal(g61,g76) = 7.85
    c: Equal(g62,g77) = 3.75
    c: PointOnObject(g74,g15)
    c: Vertical(g61,g44)
    c: Vertical(g75,g44)
    c: Coincident(g78,g38)
    c: Coincident(g79,g41)
    c: Coincident(g80,g40)
    c: Coincident(g81,g39)
    c: Radius(g78) = 2
    c: Equal(g78,g81)
    c: Equal(g78,g79)
    c: Equal(g78,g80)
    c: Horizontal(g83,g38)
    c: Horizontal(g39,g82)
    c: Equal(g78,g83)
    c: Equal(g78,g82)
    c: Coincident(g84,g11)
    c: Coincident(g84,g82)
    c: Coincident(g85,g82)
    c: Coincident(g85,g49)
    c: Equal(g85,g84)
    c: Coincident(g86,g83)
    c: Horizontal(g86)
    c: Coincident(g87,g82)
    c: Horizontal(g87)
    c: Vertical(g87,g42)
    c: Vertical(g86,g42)
    c: Equal(g86,g87)
    c: Horizontal(g88)
    c: DistanceY(g88,g44) = 20.62
    c: DistanceX(g88,g88) = 15.6
    c: Coincident(g89,g88)
    c: Horizontal(g89)
    c: Coincident(g90,g88)
    c: Horizontal(g90)
    c: PointOnObject(g90,g47)
    c: PointOnObject(g89,g45)
    c: Coincident(g91,g88)
    c: Vertical(g91)
    c: Coincident(g92,g91)
    c: Horizontal(g92)
    c: Coincident(g93,g92)
    c: Coincident(g93,g88)
    c: Vertical(g93)
    c: Equal(g89,g90)
    c: DistanceY(g91,g44) = 10.39
    c: Coincident(g94,g91)
    c: Coincident(g95,g93)
    c: Horizontal(g96)
    c: Coincident(g97,g95)
    c: Horizontal(g97)
    c: Tangent(g97,g94) = 1.5708
    c: Tangent(g96,g94) = -1.5708
    c: Tangent(g96,g95) = -1.5708
    c: DistanceY(g91,g94) = 0.5
    c: Coincident(g98,g38)
    c: Radius(g98) = 1.3
    c: Coincident(g99,g83)
    c: Coincident(g100,g41)
    c: Coincident(g101,g40)
    c: Coincident(g102,g82)
    c: Coincident(g103,g39)
    c: Equal(g98,g103)
    c: Equal(g98,g99)
    c: Equal(g98,g100)
    c: Equal(g98,g102)
    c: Equal(g98,g101)
    c: Horizontal(g104)
    c: Horizontal(g106)
    c: Vertical(g105)
    c: Vertical(g107)
    c: Tangent(g104,g108) = 1.5708
    c: Tangent(g105,g108) = 1.5708
    c: Tangent(g105,g109) = 1.5708
    c: Tangent(g106,g109) = 1.5708
    c: Tangent(g106,g110) = 1.5708
    c: Tangent(g107,g110) = 1.5708
    c: Tangent(g104,g111) = 1.5708
    c: Tangent(g107,g111) = 1.5708
    c: Equal(g111,g109)
    c: Equal(g111,g110)
    c: Radius(g111) = 0.5
    c: Coincident(g111,g44)
    c: Coincident(g108,g44)
    c: Horizontal(g106,g94)
    c: Coincident(g112,g30)
    c: Coincident(g113,g10)
    c: Coincident(g114,g31)
    c: Coincident(g115,g32)
    c: Coincident(g116,g33)
    c: Coincident(g117,g9)
    c: Coincident(g118,g8)
    c: Coincident(g119,g6)
    c: Coincident(g120,g7)
    c: Coincident(g121,g49)
    c: Coincident(g122,g48)
    c: Coincident(g123,g2)
    c: Coincident(g124,g0)
    c: Coincident(g125,g1)
    c: Coincident(g126,g3)
    c: Coincident(g127,g4)
    c: Coincident(g128,g5)
    c: Equal(g119,g123)
    c: Equal(g119,g126)
    c: Equal(g119,g127)
    c: Equal(g119,g124)
    c: Equal(g119,g125)
    c: Equal(g119,g128)
    c: Equal(g119,g120)
    c: Equal(g120,g122)
    c: Equal(g119,g118)
    c: Equal(g119,g117)
    c: Equal(g119,g116)
    c: Equal(g119,g121)
    c: Equal(g119,g113)
    c: Equal(g119,g115)
    c: Equal(g119,g112)
    c: Equal(g119,g114)
    c: Radius(g119) = 11
    c: Coincident(g129,g11)
    c: Radius(g129) = 13.5
    c: Coincident(g130,g131)
    c: Coincident(g131,g132)
    c: Coincident(g132,g133)
    c: Coincident(g133,g130)
    c: Horizontal(g130)
    c: Horizontal(g132)
    c: Vertical(g131)
    c: Vertical(g133)
    c: DistanceY(g133,g133) = 14
    c: DistanceX(g130,g130) = 14
    c: Coincident(g134,g130)
    c: Coincident(g134,g6)
    c: Coincident(g135,g132)
    c: Coincident(g135,g6)
    c: Coincident(g136,g130)
    c: Coincident(g136,g6)
    c: Equal(g134,g136)
    c: Equal(g134,g135)
    c: Coincident(g140,g142)
    c: Coincident(g142,g143)
    c: Coincident(g143,g141)
    c: Coincident(g141,g140)
    c: Horizontal(g140)
    c: Horizontal(g143)
    c: Vertical(g142)
    c: Vertical(g141)
    c: Coincident(g138,g140)
    c: Coincident(g139,g143)
    c: Coincident(g137,g140)
    c: Equal(g138,g137)
    c: Equal(g138,g139)
    c: Coincident(g138,g139)
    c: Coincident(g138,g137)
    c: Coincident(g138,g7)
    c: Coincident(g145,g146)
    c: Coincident(g146,g147)
    c: Coincident(g147,g144)
    c: Coincident(g144,g145)
    c: Horizontal(g145)
    c: Horizontal(g147)
    c: Vertical(g146)
    c: Vertical(g144)
    c: Coincident(g149,g145)
    c: Coincident(g148,g147)
    c: Coincident(g150,g145)
    c: Equal(g149,g150)
    c: Equal(g149,g148)
    c: Coincident(g148,g149)
    c: Coincident(g148,g150)
    c: Coincident(g150,g2)
    c: Coincident(g153,g154)
    c: Coincident(g154,g151)
    c: Coincident(g151,g152)
    c: Coincident(g152,g153)
    c: Horizontal(g153)
    c: Horizontal(g151)
    c: Vertical(g154)
    c: Vertical(g152)
    c: Coincident(g156,g153)
    c: Coincident(g157,g151)
    c: Coincident(g155,g153)
    c: Equal(g156,g155)
    c: Equal(g156,g157)
    c: Coincident(g157,g156)
    c: Coincident(g157,g155)
    c: Coincident(g157,g3)
    c: Coincident(g160,g161)
    c: Coincident(g161,g159)
    c: Coincident(g159,g158)
    c: Coincident(g158,g160)
    c: Horizontal(g160)
    c: Horizontal(g159)
    c: Vertical(g161)
    c: Vertical(g158)
    c: Coincident(g163,g160)
    c: Coincident(g164,g159)
    c: Coincident(g162,g160)
    c: Equal(g163,g162)
    c: Equal(g163,g164)
    c: Coincident(g164,g163)
    c: Coincident(g164,g162)
    c: Coincident(g164,g0)
    c: Coincident(g167,g168)
    c: Coincident(g168,g166)
    c: Coincident(g166,g165)
    c: Coincident(g165,g167)
    c: Horizontal(g167)
    c: Horizontal(g166)
    c: Vertical(g168)
    c: Vertical(g165)
    c: Coincident(g170,g167)
    c: Coincident(g171,g166)
    c: Coincident(g169,g167)
    c: Equal(g170,g169)
    c: Equal(g170,g171)
    c: Coincident(g171,g170)
    c: Coincident(g171,g169)
    c: Coincident(g171,g1)
    c: Coincident(g174,g175)
    c: Coincident(g175,g173)
    c: Coincident(g173,g172)
    c: Coincident(g172,g174)
    c: Horizontal(g174)
    c: Horizontal(g173)
    c: Vertical(g175)
    c: Vertical(g172)
    c: Coincident(g177,g174)
    c: Coincident(g178,g173)
    c: Coincident(g176,g174)
    c: Equal(g177,g176)
    c: Equal(g177,g178)
    c: Coincident(g178,g177)
    c: Coincident(g178,g176)
    c: Coincident(g178,g4)
    c: Coincident(g181,g182)
    c: Coincident(g182,g180)
    c: Coincident(g180,g179)
    c: Coincident(g179,g181)
    c: Horizontal(g181)
    c: Horizontal(g180)
    c: Vertical(g182)
    c: Vertical(g179)
    c: Coincident(g184,g181)
    c: Coincident(g185,g180)
    c: Coincident(g183,g181)
    c: Equal(g184,g183)
    c: Equal(g184,g185)
    c: Coincident(g185,g184)
    c: Coincident(g185,g183)
    c: Coincident(g185,g5)
    c: Coincident(g188,g189)
    c: Coincident(g189,g187)
    c: Coincident(g187,g186)
    c: Coincident(g186,g188)
    c: Horizontal(g188)
    c: Horizontal(g187)
    c: Vertical(g189)
    c: Vertical(g186)
    c: Coincident(g191,g188)
    c: Coincident(g192,g187)
    c: Coincident(g190,g188)
    c: Equal(g191,g190)
    c: Equal(g191,g192)
    c: Coincident(g192,g191)
    c: Coincident(g192,g190)
    c: Coincident(g192,g48)
    c: Coincident(g195,g196)
    c: Coincident(g196,g194)
    c: Coincident(g194,g193)
    c: Coincident(g193,g195)
    c: Horizontal(g195)
    c: Horizontal(g194)
    c: Vertical(g196)
    c: Vertical(g193)
    c: Coincident(g198,g195)
    c: Coincident(g199,g194)
    c: Coincident(g197,g195)
    c: Equal(g198,g197)
    c: Equal(g198,g199)
    c: Coincident(g199,g198)
    c: Coincident(g199,g197)
    c: Coincident(g199,g8)
    c: Coincident(g202,g203)
    c: Coincident(g203,g201)
    c: Coincident(g201,g200)
    c: Coincident(g200,g202)
    c: Horizontal(g202)
    c: Horizontal(g201)
    c: Vertical(g203)
    c: Vertical(g200)
    c: Coincident(g205,g202)
    c: Coincident(g206,g201)
    c: Coincident(g204,g202)
    c: Equal(g205,g204)
    c: Equal(g205,g206)
    c: Coincident(g206,g205)
    c: Coincident(g206,g204)
    c: Coincident(g206,g11)
    c: Coincident(g209,g210)
    c: Coincident(g210,g208)
    c: Coincident(g208,g207)
    c: Coincident(g207,g209)
    c: Horizontal(g209)
    c: Horizontal(g208)
    c: Vertical(g210)
    c: Vertical(g207)
    c: Coincident(g212,g209)
    c: Coincident(g213,g208)
    c: Coincident(g211,g209)
    c: Equal(g212,g211)
    c: Equal(g212,g213)
    c: Coincident(g213,g212)
    c: Coincident(g213,g211)
    c: Coincident(g213,g9)
    c: Coincident(g216,g217)
    c: Coincident(g217,g215)
    c: Coincident(g215,g214)
    c: Coincident(g214,g216)
    c: Horizontal(g216)
    c: Horizontal(g215)
    c: Vertical(g217)
    c: Vertical(g214)
    c: Coincident(g219,g216)
    c: Coincident(g220,g215)
    c: Coincident(g218,g216)
    c: Equal(g219,g218)
    c: Equal(g219,g220)
    c: Coincident(g220,g219)
    c: Coincident(g220,g218)
    c: Coincident(g220,g33)
    c: Coincident(g223,g224)
    c: Coincident(g224,g222)
    c: Coincident(g222,g221)
    c: Coincident(g221,g223)
    c: Horizontal(g223)
    c: Horizontal(g222)
    c: Vertical(g224)
    c: Vertical(g221)
    c: Coincident(g226,g223)
    c: Coincident(g227,g222)
    c: Coincident(g225,g223)
    c: Equal(g226,g225)
    c: Equal(g226,g227)
    c: Coincident(g227,g226)
    c: Coincident(g227,g225)
    c: Coincident(g227,g49)
    c: Coincident(g230,g231)
    c: Coincident(g231,g229)
    c: Coincident(g229,g228)
    c: Coincident(g228,g230)
    c: Horizontal(g230)
    c: Horizontal(g229)
    c: Vertical(g231)
    c: Vertical(g228)
    c: Coincident(g233,g230)
    c: Coincident(g234,g229)
    c: Coincident(g232,g230)
    c: Equal(g233,g232)
    c: Equal(g233,g234)
    c: Coincident(g234,g233)
    c: Coincident(g234,g232)
    c: Coincident(g234,g10)
    c: Coincident(g237,g238)
    c: Coincident(g238,g236)
    c: Coincident(g236,g235)
    c: Coincident(g235,g237)
    c: Horizontal(g237)
    c: Horizontal(g236)
    c: Vertical(g238)
    c: Vertical(g235)
    c: Coincident(g240,g237)
    c: Coincident(g241,g236)
    c: Coincident(g239,g237)
    c: Equal(g240,g239)
    c: Equal(g240,g241)
    c: Coincident(g241,g240)
    c: Coincident(g241,g239)
    c: Coincident(g241,g32)
    c: Coincident(g244,g245)
    c: Coincident(g245,g243)
    c: Coincident(g243,g242)
    c: Coincident(g242,g244)
    c: Horizontal(g244)
    c: Horizontal(g243)
    c: Vertical(g245)
    c: Vertical(g242)
    c: Coincident(g247,g244)
    c: Coincident(g248,g243)
    c: Coincident(g246,g244)
    c: Equal(g247,g246)
    c: Equal(g247,g248)
    c: Coincident(g248,g247)
    c: Coincident(g248,g246)
    c: Coincident(g248,g30)
    c: Coincident(g251,g252)
    c: Coincident(g252,g250)
    c: Coincident(g250,g249)
    c: Coincident(g249,g251)
    c: Horizontal(g251)
    c: Horizontal(g250)
    c: Vertical(g252)
    c: Vertical(g249)
    c: Coincident(g254,g251)
    c: Coincident(g255,g250)
    c: Coincident(g253,g251)
    c: Equal(g254,g253)
    c: Equal(g254,g255)
    c: Coincident(g255,g254)
    c: Coincident(g255,g253)
    c: Coincident(g255,g31)
    c: Equal(g133,g144)
    c: Equal(g133,g152)
    c: Equal(g133,g172)
    c: Equal(g133,g141)
    c: Equal(g133,g158)
    c: Equal(g133,g165)
    c: Equal(g133,g179)
    c: Equal(g133,g186)
    c: Equal(g133,g193)
    c: Equal(g133,g200)
    c: Equal(g133,g207)
    c: Equal(g133,g214)
    c: Equal(g133,g221)
    c: Equal(g133,g228)
    c: Equal(g133,g235)
    c: Equal(g133,g242)
    c: Equal(g133,g249)
    c: Equal(g130,g145)
    c: Equal(g130,g153)
    c: Equal(g130,g174)
    c: Equal(g130,g160)
    c: Equal(g130,g167)
    c: Equal(g130,g181)
    c: Equal(g130,g140)
    c: Equal(g130,g188)
    c: Equal(g130,g195)
    c: Equal(g130,g202)
    c: Equal(g130,g223)
    c: Equal(g130,g216)
    c: Equal(g130,g209)
    c: Equal(g130,g230)
    c: Equal(g130,g237)
    c: Equal(g130,g244)
    c: Equal(g130,g251)
    c: DistanceY(g56,g69) = 5
    c: DistanceY(g52,g68) = 5
FEATURE [Sketcher::SketchObject] Sketch001
  ExternalGeometry = -> [Sketch]
  FullyConstrained = true
  MapMode = 2
  Support = -> [Sketch]
  sketch-geometry (72):
    g0: LineSegment StartX=28.9815 StartY=84.9159 StartZ=0 EndX=28.9815 EndY=83.9159 EndZ=0
    g1: LineSegment StartX=28.9815 StartY=83.9159 StartZ=0 EndX=28.9815 EndY=82.9159 EndZ=0
    g2: LineSegment StartX=28.9815 StartY=83.9159 StartZ=0 EndX=27.9815 EndY=83.9159 EndZ=0
    g3: LineSegment StartX=28.9815 StartY=83.9159 StartZ=0 EndX=29.9815 EndY=83.9159 EndZ=0
    g4: LineSegment StartX=58.0289 StartY=92.4159 StartZ=0 EndX=58.0289 EndY=91.4159 EndZ=0
    g5: LineSegment StartX=58.0289 StartY=91.4159 StartZ=0 EndX=58.0289 EndY=90.4159 EndZ=0
    g6: LineSegment StartX=58.0289 StartY=91.4159 StartZ=0 EndX=57.0289 EndY=91.4159 EndZ=0
    g7: LineSegment StartX=58.0289 StartY=91.4159 StartZ=0 EndX=59.0289 EndY=91.4159 EndZ=0
    g8: LineSegment StartX=28.9815 StartY=54.9159 StartZ=0 EndX=28.9815 EndY=53.9159 EndZ=0
    g9: LineSegment StartX=28.9815 StartY=53.9159 StartZ=0 EndX=28.9815 EndY=52.9159 EndZ=0
    g10: LineSegment StartX=28.9815 StartY=53.9159 StartZ=0 EndX=27.9815 EndY=53.9159 EndZ=0
    g11: LineSegment StartX=28.9815 StartY=53.9159 StartZ=0 EndX=29.9815 EndY=53.9159 EndZ=0
    g12: LineSegment StartX=58.0289 StartY=62.4159 StartZ=0 EndX=58.0289 EndY=61.4159 EndZ=0
    g13: LineSegment StartX=58.0289 StartY=61.4159 StartZ=0 EndX=58.0289 EndY=60.4159 EndZ=0
    g14: LineSegment StartX=58.0289 StartY=61.4159 StartZ=0 EndX=57.0289 EndY=61.4159 EndZ=0
    g15: LineSegment StartX=58.0289 StartY=61.4159 StartZ=0 EndX=59.0289 EndY=61.4159 EndZ=0
    g16: LineSegment StartX=88.0289 StartY=92.4159 StartZ=0 EndX=88.0289 EndY=91.4159 EndZ=0
    g17: LineSegment StartX=88.0289 StartY=91.4159 StartZ=0 EndX=88.0289 EndY=90.4159 EndZ=0
    g18: LineSegment StartX=88.0289 StartY=91.4159 StartZ=0 EndX=87.0289 EndY=91.4159 EndZ=0
    g19: LineSegment StartX=88.0289 StartY=91.4159 StartZ=0 EndX=89.0289 EndY=91.4159 EndZ=0
    g20: LineSegment StartX=88.0289 StartY=62.4159 StartZ=0 EndX=88.0289 EndY=61.4159 EndZ=0
    g21: LineSegment StartX=88.0289 StartY=61.4159 StartZ=0 EndX=88.0289 EndY=60.4159 EndZ=0
    g22: LineSegment StartX=88.0289 StartY=61.4159 StartZ=0 EndX=87.0289 EndY=61.4159 EndZ=0
    g23: LineSegment StartX=88.0289 StartY=61.4159 StartZ=0 EndX=89.0289 EndY=61.4159 EndZ=0
    g24: LineSegment StartX=114.01 StartY=77.4159 StartZ=0 EndX=114.01 EndY=76.4159 EndZ=0
    g25: LineSegment StartX=114.01 StartY=76.4159 StartZ=0 EndX=114.01 EndY=75.4159 EndZ=0
    g26: LineSegment StartX=114.01 StartY=76.4159 StartZ=0 EndX=113.01 EndY=76.4159 EndZ=0
    g27: LineSegment StartX=114.01 StartY=76.4159 StartZ=0 EndX=115.01 EndY=76.4159 EndZ=0
    g28: LineSegment StartX=139.99 StartY=92.4159 StartZ=0 EndX=139.99 EndY=91.4159 EndZ=0
    g29: LineSegment StartX=139.99 StartY=91.4159 StartZ=0 EndX=139.99 EndY=90.4159 EndZ=0
    g30: LineSegment StartX=139.99 StartY=91.4159 StartZ=0 EndX=138.99 EndY=91.4159 EndZ=0
    g31: LineSegment StartX=139.99 StartY=91.4159 StartZ=0 EndX=140.99 EndY=91.4159 EndZ=0
    g32: LineSegment StartX=165.971 StartY=107.416 StartZ=0 EndX=165.971 EndY=106.416 EndZ=0
    g33: LineSegment StartX=165.971 StartY=106.416 StartZ=0 EndX=165.971 EndY=105.416 EndZ=0
    g34: LineSegment StartX=165.971 StartY=106.416 StartZ=0 EndX=164.971 EndY=106.416 EndZ=0
    g35: LineSegment StartX=165.971 StartY=106.416 StartZ=0 EndX=166.971 EndY=106.416 EndZ=0
    g36: LineSegment StartX=139.99 StartY=62.4159 StartZ=0 EndX=139.99 EndY=61.4159 EndZ=0
    g37: LineSegment StartX=139.99 StartY=61.4159 StartZ=0 EndX=139.99 EndY=60.4159 EndZ=0
    g38: LineSegment StartX=139.99 StartY=61.4159 StartZ=0 EndX=138.99 EndY=61.4159 EndZ=0
    g39: LineSegment StartX=139.99 StartY=61.4159 StartZ=0 EndX=140.99 EndY=61.4159 EndZ=0
    g40: LineSegment StartX=165.971 StartY=77.4159 StartZ=0 EndX=165.971 EndY=76.4159 EndZ=0
    g41: LineSegment StartX=165.971 StartY=76.4159 StartZ=0 EndX=165.971 EndY=75.4159 EndZ=0
    g42: LineSegment StartX=165.971 StartY=76.4159 StartZ=0 EndX=164.971 EndY=76.4159 EndZ=0
    g43: LineSegment StartX=165.971 StartY=76.4159 StartZ=0 EndX=166.971 EndY=76.4159 EndZ=0
    g44: LineSegment StartX=195.971 StartY=107.416 StartZ=0 EndX=195.971 EndY=106.416 EndZ=0
    g45: LineSegment StartX=195.971 StartY=106.416 StartZ=0 EndX=195.971 EndY=105.416 EndZ=0
    g46: LineSegment StartX=195.971 StartY=106.416 StartZ=0 EndX=194.971 EndY=106.416 EndZ=0
    g47: LineSegment StartX=195.971 StartY=106.416 StartZ=0 EndX=196.971 EndY=106.416 EndZ=0
    g48: LineSegment StartX=195.971 StartY=77.4159 StartZ=0 EndX=195.971 EndY=76.4159 EndZ=0
    g49: LineSegment StartX=195.971 StartY=76.4159 StartZ=0 EndX=195.971 EndY=75.4159 EndZ=0
    g50: LineSegment StartX=195.971 StartY=76.4159 StartZ=0 EndX=194.971 EndY=76.4159 EndZ=0
    g51: LineSegment StartX=195.971 StartY=76.4159 StartZ=0 EndX=196.971 EndY=76.4159 EndZ=0
    g52: LineSegment StartX=225.019 StartY=99.9159 StartZ=0 EndX=225.019 EndY=98.9159 EndZ=0
    g53: LineSegment StartX=225.019 StartY=98.9159 StartZ=0 EndX=225.019 EndY=97.9159 EndZ=0
    g54: LineSegment StartX=225.019 StartY=98.9159 StartZ=0 EndX=224.019 EndY=98.9159 EndZ=0
    g55: LineSegment StartX=225.019 StartY=98.9159 StartZ=0 EndX=226.019 EndY=98.9159 EndZ=0
    g56: LineSegment StartX=225.019 StartY=69.9159 StartZ=0 EndX=225.019 EndY=68.9159 EndZ=0
    g57: LineSegment StartX=225.019 StartY=68.9159 StartZ=0 EndX=225.019 EndY=67.9159 EndZ=0
    g58: LineSegment StartX=225.019 StartY=68.9159 StartZ=0 EndX=224.019 EndY=68.9159 EndZ=0
    g59: LineSegment StartX=225.019 StartY=68.9159 StartZ=0 EndX=226.019 EndY=68.9159 EndZ=0
    g60: LineSegment StartX=127 StartY=24.5841 StartZ=0 EndX=127 EndY=23.5841 EndZ=0
    g61: LineSegment StartX=127 StartY=23.5841 StartZ=0 EndX=127 EndY=22.5841 EndZ=0
    g62: LineSegment StartX=127 StartY=23.5841 StartZ=0 EndX=126 EndY=23.5841 EndZ=0
    g63: LineSegment StartX=127 StartY=23.5841 StartZ=0 EndX=128 EndY=23.5841 EndZ=0
    g64: LineSegment StartX=94.1366 StartY=26.5841 StartZ=0 EndX=95.1366 EndY=26.5841 EndZ=0
    g65: LineSegment StartX=94.1366 StartY=26.5841 StartZ=0 EndX=94.1366 EndY=25.5841 EndZ=0
    g66: LineSegment StartX=94.1366 StartY=26.5841 StartZ=0 EndX=93.1366 EndY=26.5841 EndZ=0
    g67: LineSegment StartX=94.1366 StartY=27.5841 StartZ=0 EndX=94.1366 EndY=26.5841 EndZ=0
    g68: LineSegment StartX=157.215 StartY=36.8533 StartZ=0 EndX=156.215 EndY=36.8533 EndZ=0
    g69: LineSegment StartX=157.215 StartY=36.8533 StartZ=0 EndX=158.215 EndY=36.8533 EndZ=0
    g70: LineSegment StartX=157.215 StartY=37.8533 StartZ=0 EndX=157.215 EndY=36.8533 EndZ=0
    g71: LineSegment StartX=157.215 StartY=36.8533 StartZ=0 EndX=157.215 EndY=35.8533 EndZ=0
  constraints (216):
    c: Vertical(g0)
    c: Coincident(g1,g0)
    c: Vertical(g1)
    c: Coincident(g2,g0)
    c: Horizontal(g2)
    c: Coincident(g3,g0)
    c: Horizontal(g3)
    c: Equal(g0,g2)
    c: Equal(g0,g3)
    c: Equal(g0,g1)
    c: Distance(g0) = 1
    c: Coincident(g0,g-3)
    c: Vertical(g4)
    c: Coincident(g5,g4)
    c: Vertical(g5)
    c: Coincident(g6,g4)
    c: Horizontal(g6)
    c: Coincident(g7,g4)
    c: Horizontal(g7)
    c: Equal(g4,g6)
    c: Equal(g4,g7)
    c: Equal(g4,g5)
    c: Equal(g0,g4) = 1
    c: Coincident(g7,g-4)
    c: Vertical(g8)
    c: Coincident(g9,g8)
    c: Vertical(g9)
    c: Coincident(g10,g8)
    c: Horizontal(g10)
    c: Coincident(g11,g8)
    c: Horizontal(g11)
    c: Equal(g8,g10)
    c: Equal(g8,g11)
    c: Equal(g8,g9)
    c: Equal(g0,g8) = 1
    c: Coincident(g11,g-5)
    c: Vertical(g12)
    c: Coincident(g13,g12)
    c: Vertical(g13)
    c: Coincident(g14,g12)
    c: Horizontal(g14)
    c: Coincident(g15,g12)
    c: Horizontal(g15)
    c: Equal(g12,g14)
    c: Equal(g12,g15)
    c: Equal(g12,g13)
    c: Equal(g0,g12) = 1
    c: Coincident(g15,g-6)
    c: Vertical(g16)
    c: Coincident(g17,g16)
    c: Vertical(g17)
    c: Coincident(g18,g16)
    c: Horizontal(g18)
    c: Coincident(g19,g16)
    c: Horizontal(g19)
    c: Equal(g16,g18)
    c: Equal(g16,g19)
    c: Equal(g16,g17)
    c: Equal(g0,g16) = 1
    c: Coincident(g19,g-7)
    c: Vertical(g20)
    c: Coincident(g21,g20)
    c: Vertical(g21)
    c: Coincident(g22,g20)
    c: Horizontal(g22)
    c: Coincident(g23,g20)
    c: Horizontal(g23)
    c: Equal(g20,g22)
    c: Equal(g20,g23)
    c: Equal(g20,g21)
    c: Equal(g0,g20) = 1
    c: Coincident(g23,g-8)
    c: Vertical(g24)
    c: Coincident(g25,g24)
    c: Vertical(g25)
    c: Coincident(g26,g24)
    c: Horizontal(g26)
    c: Coincident(g27,g24)
    c: Horizontal(g27)
    c: Equal(g24,g26)
    c: Equal(g24,g27)
    c: Equal(g24,g25)
    c: Equal(g0,g24) = 1
    c: Coincident(g27,g-9)
    c: Vertical(g28)
    c: Coincident(g29,g28)
    c: Vertical(g29)
    c: Coincident(g30,g28)
    c: Horizontal(g30)
    c: Coincident(g31,g28)
    c: Horizontal(g31)
    c: Equal(g28,g30)
    c: Equal(g28,g31)
    c: Equal(g28,g29)
    c: Equal(g0,g28) = 1
    c: Coincident(g31,g-12)
    c: Vertical(g32)
    c: Coincident(g33,g32)
    c: Vertical(g33)
    c: Coincident(g34,g32)
    c: Horizontal(g34)
    c: Coincident(g35,g32)
    c: Horizontal(g35)
    c: Equal(g32,g34)
    c: Equal(g32,g35)
    c: Equal(g32,g33)
    c: Equal(g0,g32) = 1
    c: Coincident(g35,g-13)
    c: Vertical(g36)
    c: Coincident(g37,g36)
    c: Vertical(g37)
    c: Coincident(g38,g36)
    c: Horizontal(g38)
    c: Coincident(g39,g36)
    c: Horizontal(g39)
    c: Equal(g36,g38)
    c: Equal(g36,g39)
    c: Equal(g36,g37)
    c: Equal(g0,g36) = 1
    c: Coincident(g39,g-10)
    c: Vertical(g40)
    c: Coincident(g41,g40)
    c: Vertical(g41)
    c: Coincident(g42,g40)
    c: Horizontal(g42)
    c: Coincident(g43,g40)
    c: Horizontal(g43)
    c: Equal(g40,g42)
    c: Equal(g40,g43)
    c: Equal(g40,g41)
    c: Equal(g0,g40) = 1
    c: Coincident(g43,g-14)
    c: Vertical(g44)
    c: Coincident(g45,g44)
    c: Vertical(g45)
    c: Coincident(g46,g44)
    c: Horizontal(g46)
    c: Coincident(g47,g44)
    c: Horizontal(g47)
    c: Equal(g44,g46)
    c: Equal(g44,g47)
    c: Equal(g44,g45)
    c: Equal(g0,g44) = 1
    c: Coincident(g47,g-15)
    c: Vertical(g48)
    c: Coincident(g49,g48)
    c: Vertical(g49)
    c: Coincident(g50,g48)
    c: Horizontal(g50)
    c: Coincident(g51,g48)
    c: Horizontal(g51)
    c: Equal(g48,g50)
    c: Equal(g48,g51)
    c: Equal(g48,g49)
    c: Equal(g0,g48) = 1
    c: Coincident(g51,g-16)
    c: Vertical(g52)
    c: Coincident(g53,g52)
    c: Vertical(g53)
    c: Coincident(g54,g52)
    c: Horizontal(g54)
    c: Coincident(g55,g52)
    c: Horizontal(g55)
    c: Equal(g52,g54)
    c: Equal(g52,g55)
    c: Equal(g52,g53)
    c: Equal(g0,g52) = 1
    c: Coincident(g55,g-17)
    c: Vertical(g56)
    c: Coincident(g57,g56)
    c: Vertical(g57)
    c: Coincident(g58,g56)
    c: Horizontal(g58)
    c: Coincident(g59,g56)
    c: Horizontal(g59)
    c: Equal(g56,g58)
    c: Equal(g56,g59)
    c: Equal(g56,g57)
    c: Equal(g0,g56) = 1
    c: Coincident(g59,g-18)
    c: Vertical(g60)
    c: Coincident(g61,g60)
    c: Vertical(g61)
    c: Coincident(g62,g60)
    c: Horizontal(g62)
    c: Coincident(g63,g60)
    c: Horizontal(g63)
    c: Equal(g60,g62)
    c: Equal(g60,g63)
    c: Equal(g60,g61)
    c: Equal(g0,g60) = 1
    c: Coincident(g63,g-11)
    c: Vertical(g67)
    c: Coincident(g65,g67)
    c: Vertical(g65)
    c: Coincident(g66,g67)
    c: Horizontal(g66)
    c: Coincident(g64,g67)
    c: Horizontal(g64)
    c: Equal(g67,g66)
    c: Equal(g67,g64)
    c: Equal(g67,g65)
    c: Equal(g0,g67) = 1
    c: Coincident(g64,g-20)
    c: Vertical(g70)
    c: Coincident(g71,g70)
    c: Vertical(g71)
    c: Coincident(g68,g70)
    c: Horizontal(g68)
    c: Coincident(g69,g70)
    c: Horizontal(g69)
    c: Equal(g70,g68)
    c: Equal(g70,g69)
    c: Equal(g70,g71)
    c: Equal(g0,g70) = 1
    c: Coincident(g71,g-19)
FEATURE [Sketcher::SketchObject] Sketch002
  ExternalGeometry = -> [Sketch]
  FullyConstrained = true
  sketch-geometry (9):
    g0: ArcOfCircle CenterX=165.971 CenterY=76.4159 CenterZ=0 NormalX=0 NormalY=0 NormalZ=1 AngleXU=0 Radius=10 StartAngle=3.83817 EndAngle=5.79323
    g1: ArcOfCircle CenterX=180.971 CenterY=68.4159 CenterZ=0 NormalX=0 NormalY=0 NormalZ=1 AngleXU=0 Radius=7 StartAngle=0.489957 EndAngle=2.65164
    g2: ArcOfCircle CenterX=195.971 CenterY=76.4159 CenterZ=0 NormalX=0 NormalY=0 NormalZ=1 AngleXU=0 Radius=10 StartAngle=3.63155 EndAngle=5.54055
    g3: ArcOfCircle CenterX=208.495 CenterY=64.92 CenterZ=0 NormalX=0 NormalY=0 NormalZ=1 AngleXU=0 Radius=7 StartAngle=0.237277 EndAngle=2.39896
    g4: ArcOfCircle CenterX=225.019 CenterY=68.9159 CenterZ=0 NormalX=0 NormalY=0 NormalZ=1 AngleXU=0 Radius=10 StartAngle=3.37887 EndAngle=5.54866
    g5: LineSegment StartX=158.301 StartY=70 StartZ=0 EndX=132.95 EndY=70 EndZ=0
    g6: LineSegment StartX=132.95 StartY=70 StartZ=0 EndX=132.95 EndY=118 EndZ=0
    g7: LineSegment StartX=132.95 StartY=118 StartZ=0 EndX=232.44 EndY=118 EndZ=0
    g8: LineSegment StartX=232.44 StartY=118 StartZ=0 EndX=232.44 EndY=62.2136 EndZ=0
  constraints (25):
    c: Coincident(g0,g-3)
    c: Coincident(g2,g-4)
    c: Coincident(g4,g-5)
    c: Tangent(g1,g0) = 1.5708
    c: Tangent(g2,g1) = 1.5708
    c: Tangent(g3,g2) = 1.5708
    c: Tangent(g4,g3) = 1.5708
    c: Equal(g0,g2)
    c: Equal(g0,g4)
    c: Equal(g1,g3)
    c: Radius(g0) = 10
    c: Radius(g1) = 7
    c: Coincident(g5,g0)
    c: Horizontal(g5)
    c: Coincident(g6,g5)
    c: Vertical(g6)
    c: Coincident(g7,g6)
    c: Horizontal(g7)
    c: Coincident(g8,g7)
    c: Coincident(g8,g4)
    c: Vertical(g8)
    c: DistanceY(g6,g6) = 48
    c: DistanceX(g7,g7) = 99.49
    c: DistanceX(g-1,g5) = 132.95
    c: DistanceY(g-1,g0) = 70
